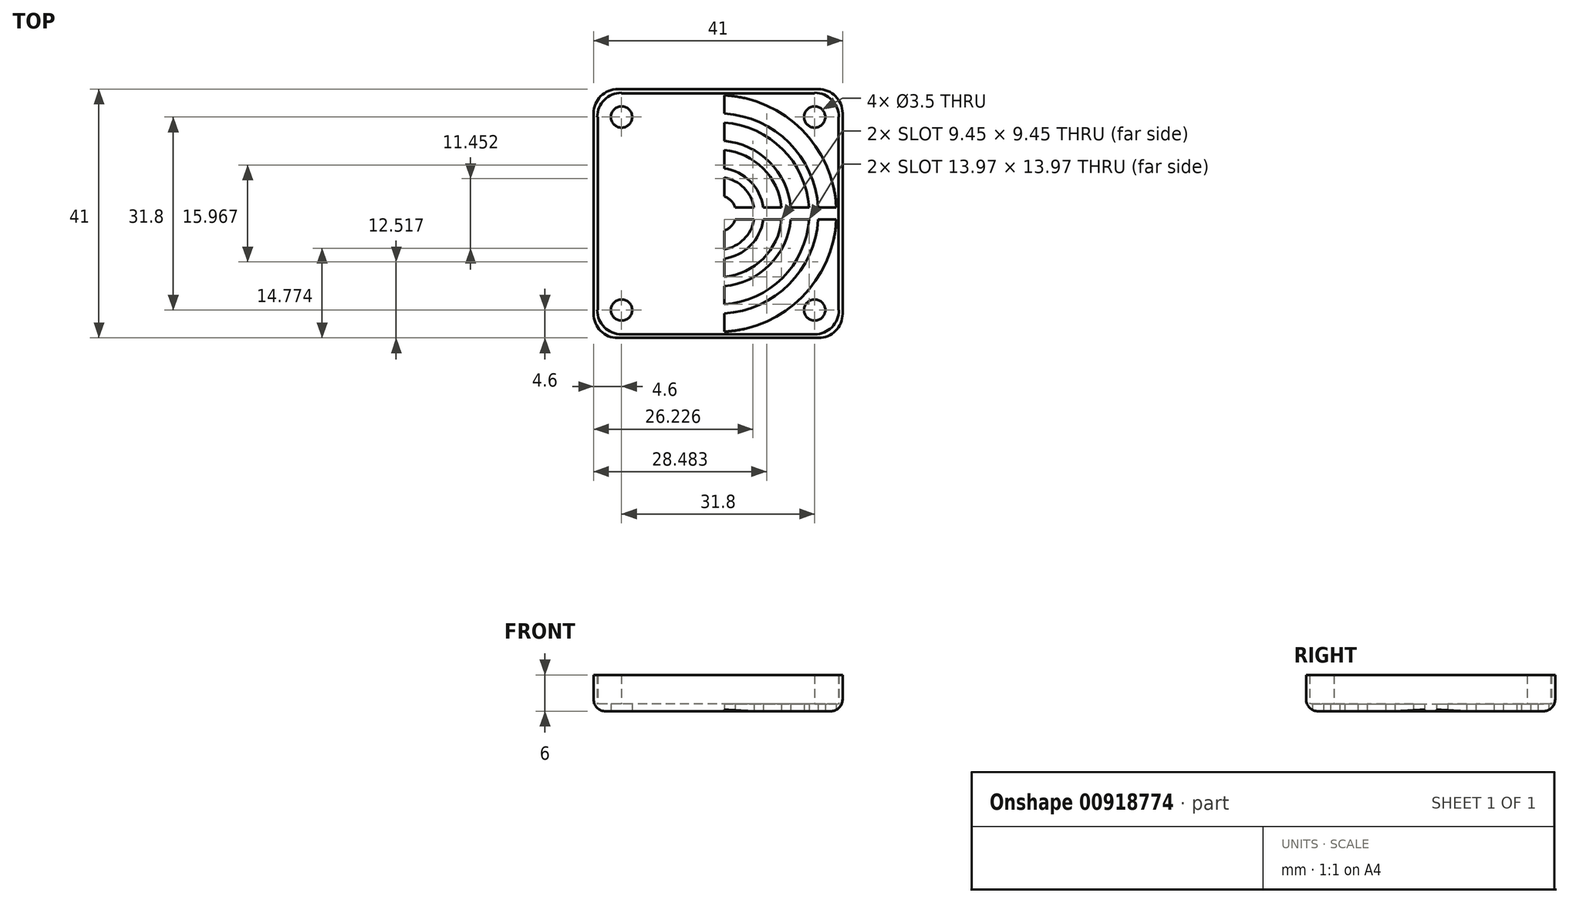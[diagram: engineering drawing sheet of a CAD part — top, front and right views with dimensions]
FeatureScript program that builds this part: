
annotation { "Feature Type Name" : "Feature", "Feature Type Description" : "" }
export const myFeature = defineFeature(function(context is Context, id is Id, definition is map)
    precondition{}
    {
        {
            var Q0;
            Q0=qCreatedBy(makeId("Top.planeOp"),FACE);
            var sketch = newSketch(context, id + "F0", { "sketchPlane" : qUnion([Q0])});
            skLineSegment(sketch, "E0.bottom", {"start": v(16.5, -20.5) * mm, "end": v(-16.5, -20.5) * mm});
            skLineSegment(sketch, "E0.top", {"start": v(16.5, 20.5) * mm, "end": v(-16.5, 20.5) * mm});
            skLineSegment(sketch, "E0.left", {"start": v(20.5, -16.5) * mm, "end": v(20.5, 16.5) * mm});
            skLineSegment(sketch, "E0.right", {"start": v(-20.5, -16.5) * mm, "end": v(-20.5, 16.5) * mm});
            skPoint(sketch, "E0.middle", {"position": v(0, 0) * mm});
            skLineSegment(sketch, "E1.bottom", {"start": v(15.9, -19.9) * mm, "end": v(-15.9, -19.9) * mm});
            skLineSegment(sketch, "E1.top", {"start": v(15.9, 19.9) * mm, "end": v(-15.9, 19.9) * mm});
            skLineSegment(sketch, "E1.left", {"start": v(19.9, -15.9) * mm, "end": v(19.9, 15.9) * mm});
            skLineSegment(sketch, "E1.right", {"start": v(-19.9, -15.9) * mm, "end": v(-19.9, 15.9) * mm});
            skCircle(sketch, "E2", {"center": v(-15.9, 15.9) * mm, "radius": 1.75 * mm});
            skCircle(sketch, "E3", {"center": v(15.9, 15.9) * mm, "radius": 1.75 * mm});
            skCircle(sketch, "E4", {"center": v(15.9, -15.9) * mm, "radius": 1.75 * mm});
            skCircle(sketch, "E5", {"center": v(-15.9, -15.9) * mm, "radius": 1.75 * mm});
            skPoint(sketch, "E6.visualSharp", {"position": v(-19.9, 19.9) * mm});
            skArc(sketch, "E6.filletArc", {"start": v(-15.9, 19.9) * mm, "mid": v(-18.73, 18.73) * mm, "end": v(-19.9, 15.9) * mm});
            skPoint(sketch, "E7.visualSharp", {"position": v(19.9, 19.9) * mm});
            skArc(sketch, "E7.filletArc", {"start": v(19.9, 15.9) * mm, "mid": v(18.73, 18.73) * mm, "end": v(15.9, 19.9) * mm});
            skPoint(sketch, "E8.visualSharp", {"position": v(19.9, -19.9) * mm});
            skArc(sketch, "E8.filletArc", {"start": v(15.9, -19.9) * mm, "mid": v(18.73, -18.73) * mm, "end": v(19.9, -15.9) * mm});
            skPoint(sketch, "E9.visualSharp", {"position": v(-19.9, -19.9) * mm});
            skArc(sketch, "E9.filletArc", {"start": v(-19.9, -15.9) * mm, "mid": v(-18.73, -18.73) * mm, "end": v(-15.9, -19.9) * mm});
            skPoint(sketch, "E10.visualSharp", {"position": v(20.5, 20.5) * mm});
            skArc(sketch, "E10.filletArc", {"start": v(20.5, 16.5) * mm, "mid": v(19.33, 19.33) * mm, "end": v(16.5, 20.5) * mm});
            skPoint(sketch, "E11.visualSharp", {"position": v(-20.5, 20.5) * mm});
            skArc(sketch, "E11.filletArc", {"start": v(-16.5, 20.5) * mm, "mid": v(-19.33, 19.33) * mm, "end": v(-20.5, 16.5) * mm});
            skPoint(sketch, "E12.visualSharp", {"position": v(-20.5, -20.5) * mm});
            skArc(sketch, "E12.filletArc", {"start": v(-20.5, -16.5) * mm, "mid": v(-19.33, -19.33) * mm, "end": v(-16.5, -20.5) * mm});
            skPoint(sketch, "E13.visualSharp", {"position": v(20.5, -20.5) * mm});
            skArc(sketch, "E13.filletArc", {"start": v(16.5, -20.5) * mm, "mid": v(19.33, -19.33) * mm, "end": v(20.5, -16.5) * mm});
            skSolve(sketch);
        }
        {
            var Q0;
            Q0=makeQuery(id+"F0.imprint","IMPRINT",FACE,{"disambiguationData":[TD([[makeQuery(id+"F0.imprint","IMPRINT",EDGE,{"derivedFrom":sQuery(id+"F0.wireOp",EDGE,"E1.bottom")}),-1.0]])]});
            extrude(context, id + "F1", {"entities" : qUnion([Q0]), "depth" : 1.2 * mm, "offsetDistance" : 25 * mm});
        }
        {
            var Q0;
            Q0 = qSketchRegion(id + "F0", true);
            extrude(context, id + "F2", {"entities" : qUnion([Q0]), "operationType" : NewBodyOperationType.ADD, "depth" : 6 * mm, "offsetDistance" : 25 * mm});
        }
        {
            var Q0;
            {var subQ0=sQuery(id+"F0.wireOp",EDGE,"E9.filletArc");var subQ1=sQuery(id+"F0.wireOp",EDGE,"E8.filletArc");var subQ2=sQuery(id+"F0.wireOp",EDGE,"E7.filletArc");var subQ3=sQuery(id+"F0.wireOp",EDGE,"E6.filletArc");var subQ4=sQuery(id+"F0.wireOp",EDGE,"E1.right");var subQ5=sQuery(id+"F0.wireOp",EDGE,"E1.left");var subQ6=sQuery(id+"F0.wireOp",EDGE,"E1.top");var subQ7=sQuery(id+"F0.wireOp",EDGE,"E1.bottom");Q0=makeQuery(id+"F2.boolean.opBoolean","MERGE",FACE,{"derivedFrom":[makeQuery(id+"F1.opExtrude","CAP_FACE",FACE,{"disambiguationData":[OSD([subQ7,subQ6,subQ5,subQ4,sQuery(id+"F0.wireOp",EDGE,"E2"),sQuery(id+"F0.wireOp",EDGE,"E3"),sQuery(id+"F0.wireOp",EDGE,"E4"),sQuery(id+"F0.wireOp",EDGE,"E5"),subQ3,subQ2,subQ1,subQ0])],"isStart":true}),makeQuery(id+"F2.opExtrude","CAP_FACE",FACE,{"disambiguationData":[OSD([sQuery(id+"F0.wireOp",EDGE,"E0.bottom"),sQuery(id+"F0.wireOp",EDGE,"E0.top"),sQuery(id+"F0.wireOp",EDGE,"E0.left"),sQuery(id+"F0.wireOp",EDGE,"E0.right"),subQ7,subQ6,subQ5,subQ4,subQ3,subQ2,subQ1,subQ0,sQuery(id+"F0.wireOp",EDGE,"E10.filletArc"),sQuery(id+"F0.wireOp",EDGE,"E11.filletArc"),sQuery(id+"F0.wireOp",EDGE,"E12.filletArc"),sQuery(id+"F0.wireOp",EDGE,"E13.filletArc")])],"isStart":true})]});}
            var sketch = newSketch(context, id + "F3", { "sketchPlane" : qUnion([Q0])});
            skCircle(sketch, "E14", {"center": v(0, 0) * mm, "radius": 1.5 * mm});
            skArc(sketch, "E15", {"start": v(-1, 2.83) * mm, "mid": v(-3, 0) * mm, "end": v(-1, -2.83) * mm});
            skArc(sketch, "E16", {"start": v(1, -5.92) * mm, "mid": v(0, 6) * mm, "end": v(-1, -5.92) * mm});
            skArc(sketch, "E17", {"start": v(-1, 7.43) * mm, "mid": v(-7.5, 0) * mm, "end": v(-1, -7.43) * mm});
            skArc(sketch, "E18", {"start": v(-1, 10.45) * mm, "mid": v(-10.5, 0) * mm, "end": v(-1, -10.45) * mm});
            skArc(sketch, "E19", {"start": v(-1, 11.96) * mm, "mid": v(-12, 0) * mm, "end": v(-1, -11.96) * mm});
            skArc(sketch, "E20", {"start": v(1, -14.97) * mm, "mid": v(0, 15) * mm, "end": v(-1, -14.97) * mm});
            skArc(sketch, "E21", {"start": v(-1, 16.47) * mm, "mid": v(-16.5, 0) * mm, "end": v(-1, -16.47) * mm});
            skCircle(sketch, "E22", {"center": v(0, 0) * mm, "radius": 19.5 * mm});
            skLineSegment(sketch, "E23.bottom", {"start": v(19.5, 0) * mm, "end": v(19.47, 0) * mm});
            skLineSegment(sketch, "E23.top", {"start": v(19.5, 0) * mm, "end": v(19.47, 0) * mm});
            skLineSegment(sketch, "E23.left", {"start": v(19.5, 0) * mm, "end": v(19.5, 0) * mm});
            skLineSegment(sketch, "E23.right", {"start": v(-19.5, 0) * mm, "end": v(-19.5, 0) * mm});
            skLineSegment(sketch, "E24.bottom", {"start": v(1, 19.47) * mm, "end": v(-1, 19.47) * mm});
            skLineSegment(sketch, "E24.top", {"start": v(1, -19.47) * mm, "end": v(-1, -19.47) * mm});
            skLineSegment(sketch, "E24.left", {"start": v(1, 19.47) * mm, "end": v(1, -19.47) * mm});
            skLineSegment(sketch, "E24.right", {"start": v(-1, 19.47) * mm, "end": v(-1, -19.47) * mm});
            skLineSegment(sketch, "E25.bottom", {"start": v(19.47, -1) * mm, "end": v(-19.47, -1) * mm});
            skLineSegment(sketch, "E25.top", {"start": v(19.47, 1) * mm, "end": v(-19.47, 1) * mm});
            skLineSegment(sketch, "E25.left", {"start": v(19.47, -1) * mm, "end": v(19.47, 1) * mm});
            skLineSegment(sketch, "E25.right", {"start": v(-19.47, -1) * mm, "end": v(-19.47, 1) * mm});
            skLineSegment(sketch, "E26.trimOffspring", {"start": v(-19.47, 0) * mm, "end": v(-19.5, 0) * mm});
            skArc(sketch, "E27.trimOffspring", {"start": v(1, -2.83) * mm, "mid": v(3, 0) * mm, "end": v(1, 2.83) * mm});
            skArc(sketch, "E28.trimOffspring", {"start": v(1, -7.43) * mm, "mid": v(7.5, 0) * mm, "end": v(1, 7.43) * mm});
            skArc(sketch, "E29.trimOffspring", {"start": v(1, -10.45) * mm, "mid": v(10.5, 0) * mm, "end": v(1, 10.45) * mm});
            skArc(sketch, "E30.trimOffspring", {"start": v(1, -11.96) * mm, "mid": v(12, 0) * mm, "end": v(1, 11.96) * mm});
            skArc(sketch, "E31.trimOffspring", {"start": v(1, -16.47) * mm, "mid": v(16.5, 0) * mm, "end": v(1, 16.47) * mm});
            skSolve(sketch);
        }
        {
            var Q0;
            {var subQ0=sQuery(id+"F3.wireOp",EDGE,"E24.left");var subQ5=sQuery(id+"F3.wireOp",EDGE,"E31.trimOffspring");var subQ6=makeQuery(id+"F3.imprint","INTERSECT",VERTEX,{"disambiguationData":[OD(1.0)],"derivedFrom":[subQ0,subQ5]});Q0=makeQuery(id+"F3.imprint","IMPRINT",FACE,{"disambiguationData":[TD([[makeQuery(id+"F3.imprint","IMPRINT",EDGE,{"disambiguationData":[TD([[subQ6,1.0]])],"derivedFrom":subQ5}),-1.0]])]});}
            var Q1;
            {var subQ0=sQuery(id+"F3.wireOp",EDGE,"E24.right");var subQ1=sQuery(id+"F3.wireOp",EDGE,"E21");var subQ2=makeQuery(id+"F3.imprint","INTERSECT",VERTEX,{"disambiguationData":[OD(0.0)],"derivedFrom":[subQ1,subQ0]});Q1=makeQuery(id+"F3.imprint","IMPRINT",FACE,{"disambiguationData":[TD([[makeQuery(id+"F3.imprint","IMPRINT",EDGE,{"disambiguationData":[TD([[subQ2,-1.0]])],"derivedFrom":subQ1}),-1.0]])]});}
            var Q2;
            {var subQ0=sQuery(id+"F3.wireOp",EDGE,"E24.right");var subQ1=sQuery(id+"F3.wireOp",EDGE,"E21");var subQ2=makeQuery(id+"F3.imprint","INTERSECT",VERTEX,{"disambiguationData":[OD(1.0)],"derivedFrom":[subQ1,subQ0]});Q2=makeQuery(id+"F3.imprint","IMPRINT",FACE,{"disambiguationData":[TD([[makeQuery(id+"F3.imprint","IMPRINT",EDGE,{"disambiguationData":[TD([[subQ2,1.0]])],"derivedFrom":subQ1}),-1.0]])]});}
            var Q3;
            {var subQ0=sQuery(id+"F3.wireOp",EDGE,"E24.left");var subQ5=sQuery(id+"F3.wireOp",EDGE,"E31.trimOffspring");var subQ6=makeQuery(id+"F3.imprint","INTERSECT",VERTEX,{"disambiguationData":[OD(0.0)],"derivedFrom":[subQ0,subQ5]});Q3=makeQuery(id+"F3.imprint","IMPRINT",FACE,{"disambiguationData":[TD([[makeQuery(id+"F3.imprint","IMPRINT",EDGE,{"disambiguationData":[TD([[subQ6,-1.0]])],"derivedFrom":subQ5}),-1.0]])]});}
            var Q4;
            {var subQ0=sQuery(id+"F3.wireOp",EDGE,"E24.left");var subQ1=sQuery(id+"F3.wireOp",EDGE,"E20");var subQ2=makeQuery(id+"F3.imprint","INTERSECT",VERTEX,{"disambiguationData":[OD(0.0)],"derivedFrom":[subQ1,subQ0]});Q4=makeQuery(id+"F3.imprint","IMPRINT",FACE,{"disambiguationData":[TD([[makeQuery(id+"F3.imprint","IMPRINT",EDGE,{"disambiguationData":[TD([[subQ2,-1.0]])],"derivedFrom":subQ1}),1.0]])]});}
            var Q5;
            {var subQ0=sQuery(id+"F3.wireOp",EDGE,"E24.right");var subQ1=sQuery(id+"F3.wireOp",EDGE,"E19");var subQ2=makeQuery(id+"F3.imprint","INTERSECT",VERTEX,{"disambiguationData":[OD(1.0)],"derivedFrom":[subQ1,subQ0]});Q5=makeQuery(id+"F3.imprint","IMPRINT",FACE,{"disambiguationData":[TD([[makeQuery(id+"F3.imprint","IMPRINT",EDGE,{"disambiguationData":[TD([[subQ2,1.0]])],"derivedFrom":subQ1}),-1.0]])]});}
            var Q6;
            {var subQ0=sQuery(id+"F3.wireOp",EDGE,"E24.right");var subQ1=sQuery(id+"F3.wireOp",EDGE,"E19");var subQ2=makeQuery(id+"F3.imprint","INTERSECT",VERTEX,{"disambiguationData":[OD(0.0)],"derivedFrom":[subQ1,subQ0]});Q6=makeQuery(id+"F3.imprint","IMPRINT",FACE,{"disambiguationData":[TD([[makeQuery(id+"F3.imprint","IMPRINT",EDGE,{"disambiguationData":[TD([[subQ2,-1.0]])],"derivedFrom":subQ1}),-1.0]])]});}
            var Q7;
            {var subQ0=sQuery(id+"F3.wireOp",EDGE,"E24.right");var subQ1=sQuery(id+"F3.wireOp",EDGE,"E17");var subQ2=makeQuery(id+"F3.imprint","INTERSECT",VERTEX,{"disambiguationData":[OD(0.0)],"derivedFrom":[subQ1,subQ0]});Q7=makeQuery(id+"F3.imprint","IMPRINT",FACE,{"disambiguationData":[TD([[makeQuery(id+"F3.imprint","IMPRINT",EDGE,{"disambiguationData":[TD([[subQ2,-1.0]])],"derivedFrom":subQ1}),-1.0]])]});}
            var Q8;
            {var subQ0=sQuery(id+"F3.wireOp",EDGE,"E24.right");var subQ1=sQuery(id+"F3.wireOp",EDGE,"E17");var subQ2=makeQuery(id+"F3.imprint","INTERSECT",VERTEX,{"disambiguationData":[OD(1.0)],"derivedFrom":[subQ1,subQ0]});Q8=makeQuery(id+"F3.imprint","IMPRINT",FACE,{"disambiguationData":[TD([[makeQuery(id+"F3.imprint","IMPRINT",EDGE,{"disambiguationData":[TD([[subQ2,1.0]])],"derivedFrom":subQ1}),-1.0]])]});}
            var Q9;
            {var subQ0=sQuery(id+"F3.wireOp",EDGE,"E28.trimOffspring");var subQ1=sQuery(id+"F3.wireOp",EDGE,"E24.left");var subQ2=makeQuery(id+"F3.imprint","INTERSECT",VERTEX,{"disambiguationData":[OD(0.0)],"derivedFrom":[subQ1,subQ0]});Q9=makeQuery(id+"F3.imprint","IMPRINT",FACE,{"disambiguationData":[TD([[makeQuery(id+"F3.imprint","IMPRINT",EDGE,{"disambiguationData":[TD([[subQ2,-1.0]])],"derivedFrom":subQ1}),1.0]])]});}
            var Q10;
            {var subQ0=sQuery(id+"F3.wireOp",EDGE,"E24.left");var subQ1=sQuery(id+"F3.wireOp",EDGE,"E16");var subQ2=makeQuery(id+"F3.imprint","INTERSECT",VERTEX,{"disambiguationData":[OD(0.0)],"derivedFrom":[subQ1,subQ0]});Q10=makeQuery(id+"F3.imprint","IMPRINT",FACE,{"disambiguationData":[TD([[makeQuery(id+"F3.imprint","IMPRINT",EDGE,{"disambiguationData":[TD([[subQ2,-1.0]])],"derivedFrom":subQ1}),1.0]])]});}
            var Q11;
            {var subQ0=sQuery(id+"F3.wireOp",EDGE,"E24.right");var subQ1=sQuery(id+"F3.wireOp",EDGE,"E15");var subQ2=makeQuery(id+"F3.imprint","INTERSECT",VERTEX,{"disambiguationData":[OD(1.0)],"derivedFrom":[subQ1,subQ0]});Q11=makeQuery(id+"F3.imprint","IMPRINT",FACE,{"disambiguationData":[TD([[makeQuery(id+"F3.imprint","IMPRINT",EDGE,{"disambiguationData":[TD([[subQ2,1.0]])],"derivedFrom":subQ1}),-1.0]])]});}
            var Q12;
            {var subQ0=sQuery(id+"F3.wireOp",EDGE,"E24.right");var subQ1=sQuery(id+"F3.wireOp",EDGE,"E15");var subQ2=makeQuery(id+"F3.imprint","INTERSECT",VERTEX,{"disambiguationData":[OD(0.0)],"derivedFrom":[subQ1,subQ0]});Q12=makeQuery(id+"F3.imprint","IMPRINT",FACE,{"disambiguationData":[TD([[makeQuery(id+"F3.imprint","IMPRINT",EDGE,{"disambiguationData":[TD([[subQ2,-1.0]])],"derivedFrom":subQ1}),-1.0]])]});}
            var Q13;
            {var subQ0=sQuery(id+"F3.wireOp",EDGE,"E25.top");var subQ1=sQuery(id+"F3.wireOp",EDGE,"E16");var subQ2=makeQuery(id+"F3.imprint","INTERSECT",VERTEX,{"disambiguationData":[OD(0.0)],"derivedFrom":[subQ1,subQ0]});Q13=makeQuery(id+"F3.imprint","IMPRINT",FACE,{"disambiguationData":[TD([[makeQuery(id+"F3.imprint","IMPRINT",EDGE,{"disambiguationData":[TD([[subQ2,-1.0]])],"derivedFrom":subQ1}),1.0]])]});}
            var Q14;
            {var subQ0=sQuery(id+"F3.wireOp",EDGE,"E28.trimOffspring");var subQ1=sQuery(id+"F3.wireOp",EDGE,"E24.left");var subQ2=makeQuery(id+"F3.imprint","INTERSECT",VERTEX,{"disambiguationData":[OD(1.0)],"derivedFrom":[subQ1,subQ0]});Q14=makeQuery(id+"F3.imprint","IMPRINT",FACE,{"disambiguationData":[TD([[makeQuery(id+"F3.imprint","IMPRINT",EDGE,{"disambiguationData":[TD([[subQ2,1.0]])],"derivedFrom":subQ1}),1.0]])]});}
            var Q15;
            {var subQ0=sQuery(id+"F3.wireOp",EDGE,"E25.top");var subQ1=sQuery(id+"F3.wireOp",EDGE,"E20");var subQ2=makeQuery(id+"F3.imprint","INTERSECT",VERTEX,{"disambiguationData":[OD(0.0)],"derivedFrom":[subQ1,subQ0]});Q15=makeQuery(id+"F3.imprint","IMPRINT",FACE,{"disambiguationData":[TD([[makeQuery(id+"F3.imprint","IMPRINT",EDGE,{"disambiguationData":[TD([[subQ2,-1.0]])],"derivedFrom":subQ1}),1.0]])]});}
            extrude(context, id + "F4", {"entities" : qUnion([Q0, Q1, Q2, Q3, Q4, Q5, Q6, Q7, Q8, Q9, Q10, Q11, Q12, Q13, Q14, Q15]), "operationType" : NewBodyOperationType.REMOVE, "oppositeDirection" : true, "depth" : 10 * mm, "offsetDistance" : 25 * mm});
        }
        {
            var Q0;
            Q0=makeQuery(id+"F2.opExtrude","CAP_EDGE",EDGE,{"disambiguationData":[OSD([sQuery(id+"F0.wireOp",EDGE,"E0.bottom")])],"isStart":true});
            var Q1;
            Q1=makeQuery(id+"F2.opExtrude","CAP_EDGE",EDGE,{"disambiguationData":[OSD([sQuery(id+"F0.wireOp",EDGE,"E12.filletArc")])],"isStart":true});
            var Q2;
            Q2=makeQuery(id+"F2.opExtrude","CAP_EDGE",EDGE,{"disambiguationData":[OSD([sQuery(id+"F0.wireOp",EDGE,"E13.filletArc")])],"isStart":true});
            var Q3;
            Q3=makeQuery(id+"F2.opExtrude","CAP_EDGE",EDGE,{"disambiguationData":[OSD([sQuery(id+"F0.wireOp",EDGE,"E0.top")])],"isStart":true});
            var Q4;
            Q4=makeQuery(id+"F2.opExtrude","CAP_EDGE",EDGE,{"disambiguationData":[OSD([sQuery(id+"F0.wireOp",EDGE,"E10.filletArc")])],"isStart":true});
            var Q5;
            Q5=makeQuery(id+"F2.opExtrude","CAP_EDGE",EDGE,{"disambiguationData":[OSD([sQuery(id+"F0.wireOp",EDGE,"E11.filletArc")])],"isStart":true});
            var Q6;
            Q6=makeQuery(id+"F2.opExtrude","CAP_EDGE",EDGE,{"disambiguationData":[OSD([sQuery(id+"F0.wireOp",EDGE,"E0.right")])],"isStart":true});
            var Q7;
            Q7=makeQuery(id+"F2.opExtrude","CAP_EDGE",EDGE,{"disambiguationData":[OSD([sQuery(id+"F0.wireOp",EDGE,"E0.left")])],"isStart":true});
            fillet(context, id + "F5", {"entities" : qUnion([Q0, Q1, Q2, Q3, Q4, Q5, Q6, Q7]), "radius" : 2 * mm, "tangentPropagation" : true, "allowEdgeOverflow" : false});
        }
        {
            var Q0;
            Q0=makeQuery(id+"F2.opExtrude","SWEPT_FACE",FACE,{"disambiguationData":[OSD([sQuery(id+"F0.wireOp",EDGE,"E1.left")])]});
            extrude(context, id + "F6", {"entities" : qUnion([Q0]), "operationType" : NewBodyOperationType.ADD, "depth" : .1 * mm, "offsetDistance" : 25 * mm});
        }
        {
            var Q0;
            Q0=makeQuery(id+"F2.opExtrude","SWEPT_FACE",FACE,{"disambiguationData":[OSD([sQuery(id+"F0.wireOp",EDGE,"E1.right")])]});
            extrude(context, id + "F7", {"entities" : qUnion([Q0]), "operationType" : NewBodyOperationType.ADD, "depth" : .1 * mm, "offsetDistance" : 25 * mm});
        }
        {
            var Q0;
            Q0=makeQuery(id+"F2.opExtrude","SWEPT_FACE",FACE,{"disambiguationData":[OSD([sQuery(id+"F0.wireOp",EDGE,"E1.top")])]});
            extrude(context, id + "F8", {"entities" : qUnion([Q0]), "operationType" : NewBodyOperationType.ADD, "depth" : .1 * mm, "offsetDistance" : 25 * mm});
        }
    });
